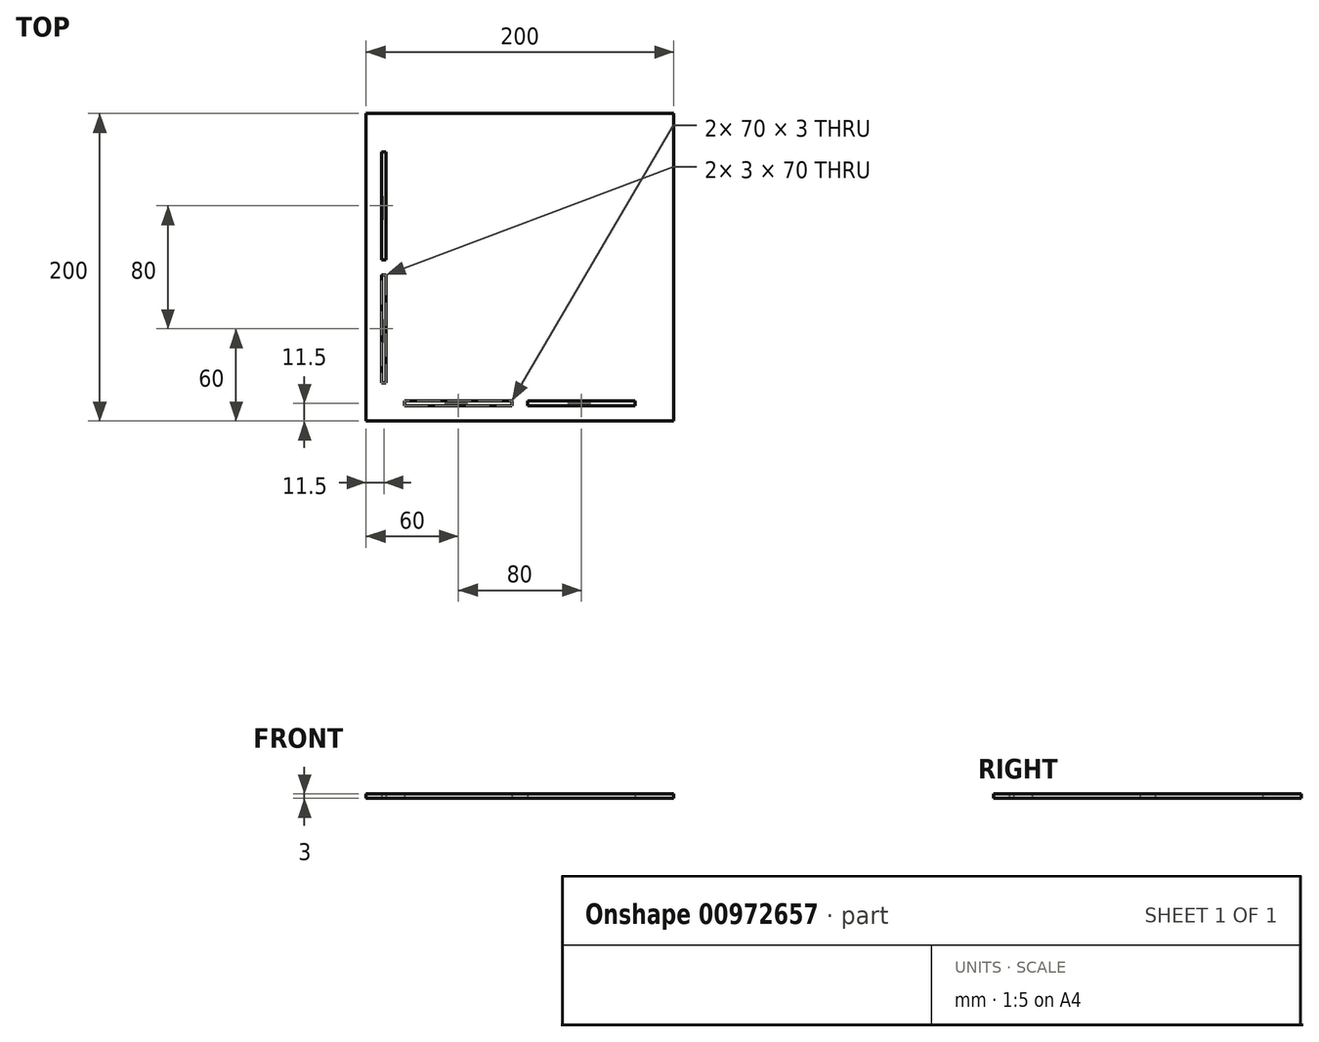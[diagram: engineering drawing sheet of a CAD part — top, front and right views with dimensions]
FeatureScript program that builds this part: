
annotation { "Feature Type Name" : "Feature", "Feature Type Description" : "" }
export const myFeature = defineFeature(function(context is Context, id is Id, definition is map)
    precondition{}
    {
        {
            var Q0;
            Q0=qCreatedBy(makeId("Top.planeOp"),FACE);
            var sketch = newSketch(context, id + "F0", { "sketchPlane" : qUnion([Q0])});
            skLineSegment(sketch, "E0.bottom", {"start": v(0, 200) * mm, "end": v(200, 200) * mm});
            skLineSegment(sketch, "E0.top", {"start": v(0, 0) * mm, "end": v(200, 0) * mm});
            skLineSegment(sketch, "E0.left", {"start": v(0, 200) * mm, "end": v(0, 0) * mm});
            skLineSegment(sketch, "E0.right", {"start": v(200, 200) * mm, "end": v(200, 0) * mm});
            skPoint(sketch, "E1", {"position": v(0, 100) * mm});
            skPoint(sketch, "E2", {"position": v(100, 0) * mm});
            skLineSegment(sketch, "E3.bottom", {"start": v(25, 10) * mm, "end": v(95, 10) * mm});
            skLineSegment(sketch, "E3.top", {"start": v(25, 13) * mm, "end": v(95, 13) * mm});
            skLineSegment(sketch, "E3.left", {"start": v(25, 10) * mm, "end": v(25, 13) * mm});
            skLineSegment(sketch, "E3.right", {"start": v(95, 10) * mm, "end": v(95, 13) * mm});
            skLineSegment(sketch, "E4.bottom", {"start": v(105, 10) * mm, "end": v(175, 10) * mm});
            skLineSegment(sketch, "E4.top", {"start": v(105, 13) * mm, "end": v(175, 13) * mm});
            skLineSegment(sketch, "E4.left", {"start": v(105, 10) * mm, "end": v(105, 13) * mm});
            skLineSegment(sketch, "E4.right", {"start": v(175, 10) * mm, "end": v(175, 13) * mm});
            skLineSegment(sketch, "E5.bottom", {"start": v(10, 175) * mm, "end": v(13, 175) * mm});
            skLineSegment(sketch, "E5.top", {"start": v(10, 105) * mm, "end": v(13, 105) * mm});
            skLineSegment(sketch, "E5.left", {"start": v(10, 175) * mm, "end": v(10, 105) * mm});
            skLineSegment(sketch, "E5.right", {"start": v(13, 175) * mm, "end": v(13, 105) * mm});
            skLineSegment(sketch, "E6.bottom", {"start": v(10, 95) * mm, "end": v(13, 95) * mm});
            skLineSegment(sketch, "E6.top", {"start": v(10, 25) * mm, "end": v(13, 25) * mm});
            skLineSegment(sketch, "E6.left", {"start": v(10, 95) * mm, "end": v(10, 25) * mm});
            skLineSegment(sketch, "E6.right", {"start": v(13, 95) * mm, "end": v(13, 25) * mm});
            skSolve(sketch);
        }
        {
            var Q0;
            Q0=makeQuery(id+"F0.imprint","IMPRINT",FACE,{"disambiguationData":[TD([[makeQuery(id+"F0.imprint","IMPRINT",EDGE,{"derivedFrom":sQuery(id+"F0.wireOp",EDGE,"E0.bottom")}),-1.0]])]});
            extrude(context, id + "F1", {"entities" : qUnion([Q0]), "depth" : 3 * mm, "offsetDistance" : 25 * mm});
        }
    });
